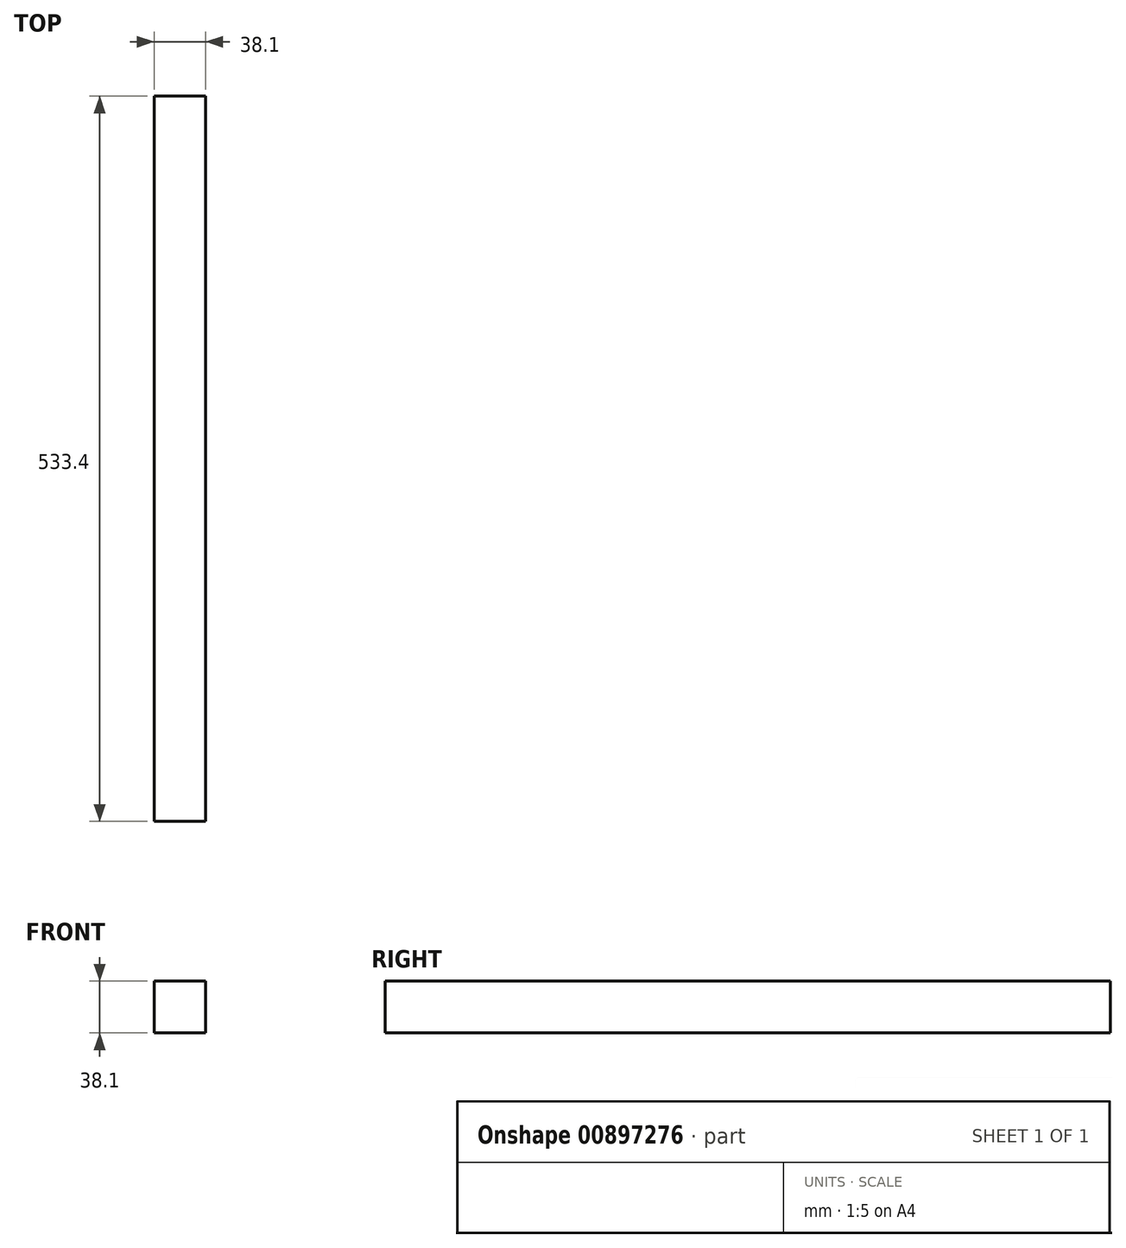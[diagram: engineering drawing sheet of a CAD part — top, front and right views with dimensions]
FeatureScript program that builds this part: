
annotation { "Feature Type Name" : "Feature", "Feature Type Description" : "" }
export const myFeature = defineFeature(function(context is Context, id is Id, definition is map)
    precondition{}
    {
        {
            var Q0;
            Q0=qCreatedBy(makeId("Front.planeOp"),FACE);
            var sketch = newSketch(context, id + "F0", { "sketchPlane" : qUnion([Q0])});
            skLineSegment(sketch, "E0.bottom", {"start": v(-19.05, 19.05) * mm, "end": v(19.05, 19.05) * mm});
            skLineSegment(sketch, "E0.top", {"start": v(-19.05, -19.05) * mm, "end": v(19.05, -19.05) * mm});
            skLineSegment(sketch, "E0.left", {"start": v(-19.05, 19.05) * mm, "end": v(-19.05, -19.05) * mm});
            skLineSegment(sketch, "E0.right", {"start": v(19.05, 19.05) * mm, "end": v(19.05, -19.05) * mm});
            skPoint(sketch, "E0.middle", {"position": v(0, 0) * mm});
            skSolve(sketch);
        }
        {
            var Q0;
            Q0=makeQuery(id+"F0.imprint","IMPRINT",FACE,{"disambiguationData":[TD([[makeQuery(id+"F0.imprint","IMPRINT",EDGE,{"derivedFrom":sQuery(id+"F0.wireOp",EDGE,"E0.bottom")}),-1.0]])]});
            extrude(context, id + "F1", {"entities" : qUnion([Q0]), "depth" : 533.4 * mm, "offsetDistance" : 25.4 * mm});
        }
    });
